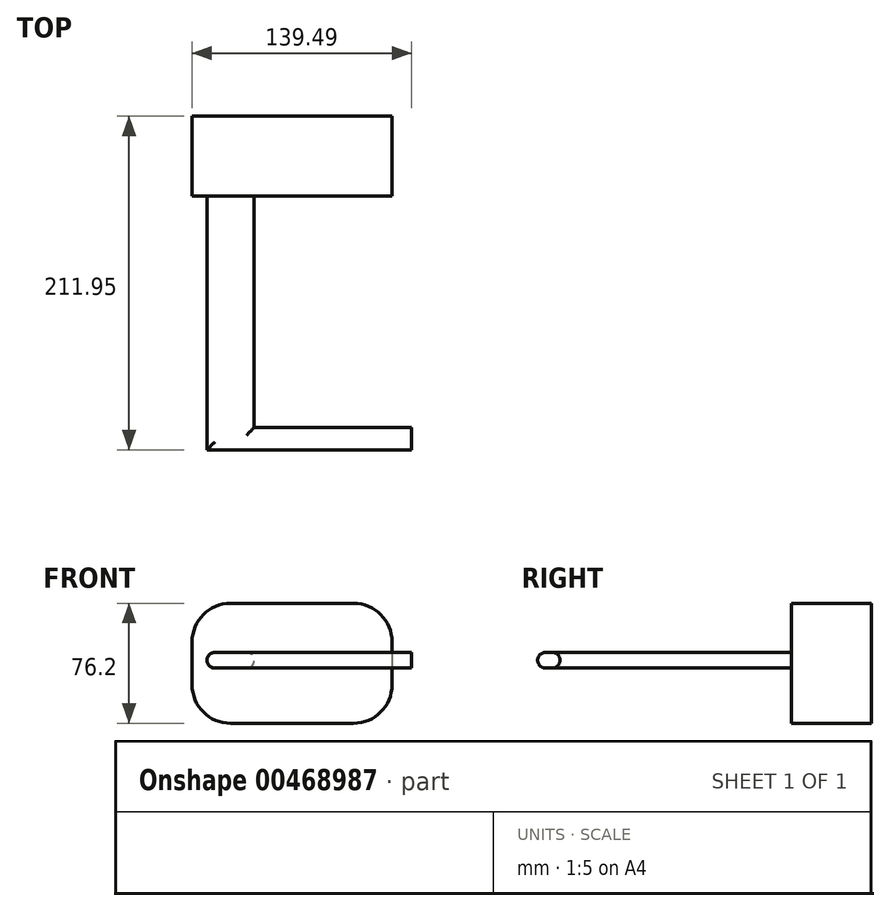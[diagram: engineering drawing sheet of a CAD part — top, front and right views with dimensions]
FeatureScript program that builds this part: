
annotation { "Feature Type Name" : "Feature", "Feature Type Description" : "" }
export const myFeature = defineFeature(function(context is Context, id is Id, definition is map)
    precondition{}
    {
        {
            var Q0;
            Q0=qCreatedBy(makeId("Front.planeOp"),FACE);
            var sketch = newSketch(context, id + "F0", { "sketchPlane" : qUnion([Q0])});
            skLineSegment(sketch, "E0.bottom", {"start": v(-41.85, 70.88) * mm, "end": v(85.15, 70.88) * mm});
            skLineSegment(sketch, "E0.top", {"start": v(-41.85, -5.32) * mm, "end": v(85.15, -5.32) * mm});
            skLineSegment(sketch, "E0.left", {"start": v(-41.85, 70.88) * mm, "end": v(-41.85, -5.32) * mm});
            skLineSegment(sketch, "E0.right", {"start": v(85.15, 70.88) * mm, "end": v(85.15, -5.32) * mm});
            skPoint(sketch, "E0.middle", {"position": v(21.65, 32.78) * mm});
            skSolve(sketch);
        }
        {
            var Q0;
            Q0=makeQuery(id+"F0.imprint","IMPRINT",FACE,{"disambiguationData":[TD([[makeQuery(id+"F0.imprint","IMPRINT",EDGE,{"derivedFrom":sQuery(id+"F0.wireOp",EDGE,"E0.bottom")}),-1.0]])]});
            extrude(context, id + "F1", {"entities" : qUnion([Q0]), "depth" : 50.8 * mm});
        }
        {
            var Q0;
            Q0=makeQuery(id+"F1.opExtrude","SWEPT_EDGE",EDGE,{"disambiguationData":[OSD([sQuery(id+"F0.wireOp",EDGE,"E0.bottom"),sQuery(id+"F0.wireOp",EDGE,"E0.left")])]});
            var Q1;
            Q1=makeQuery(id+"F1.opExtrude","SWEPT_EDGE",EDGE,{"disambiguationData":[OSD([sQuery(id+"F0.wireOp",EDGE,"E0.top"),sQuery(id+"F0.wireOp",EDGE,"E0.left")])]});
            var Q2;
            Q2=makeQuery(id+"F1.opExtrude","SWEPT_EDGE",EDGE,{"disambiguationData":[OSD([sQuery(id+"F0.wireOp",EDGE,"E0.top"),sQuery(id+"F0.wireOp",EDGE,"E0.right")])]});
            var Q3;
            Q3=makeQuery(id+"F1.opExtrude","SWEPT_EDGE",EDGE,{"disambiguationData":[OSD([sQuery(id+"F0.wireOp",EDGE,"E0.bottom"),sQuery(id+"F0.wireOp",EDGE,"E0.right")])]});
            fillet(context, id + "F2", {"entities" : qUnion([Q0, Q1, Q2, Q3]), "radius" : 24.44 * mm, "tangentPropagation" : true, "allowEdgeOverflow" : false});
        }
        {
            var Q0;
            Q0=makeQuery(id+"F1.opExtrude","CAP_FACE",FACE,{"disambiguationData":[OSD([sQuery(id+"F0.wireOp",EDGE,"E0.bottom"),sQuery(id+"F0.wireOp",EDGE,"E0.top"),sQuery(id+"F0.wireOp",EDGE,"E0.left"),sQuery(id+"F0.wireOp",EDGE,"E0.right")])],"isStart":true});
            var sketch = newSketch(context, id + "F3", { "sketchPlane" : qUnion([Q0])});
            skCircle(sketch, "E1", {"center": v(-21.77, 13.37) * mm, "radius": 18.7 * mm});
            skSolve(sketch);
        }
        {
            var Q0;
            {var subQ6=sQuery(id+"F3.wireOp",EDGE,"E1");Q0=makeQuery(id+"F3.imprint","IMPRINT",FACE,{"disambiguationData":[TD([[makeQuery(id+"F3.imprint","IMPRINT",EDGE,{"derivedFrom":subQ6}),-1.0]])]});}
            var sketch = newSketch(context, id + "F4", { "sketchPlane" : qUnion([Q0])});
            skLineSegment(sketch, "E2.bottom", {"start": v(2.36, 39.76) * mm, "end": v(32.36, 39.76) * mm});
            skLineSegment(sketch, "E2.top", {"start": v(2.36, 29.76) * mm, "end": v(32.36, 29.76) * mm});
            skLineSegment(sketch, "E2.left", {"start": v(2.36, 39.76) * mm, "end": v(2.36, 29.76) * mm});
            skLineSegment(sketch, "E2.right", {"start": v(32.36, 39.76) * mm, "end": v(32.36, 29.76) * mm});
            skSolve(sketch);
        }
        {
            var Q0;
            Q0 = qSketchRegion(id + "F4", true);
            var Q1;
            Q1=makeQuery(id+"F4.imprint","IMPRINT",FACE,{"disambiguationData":[TD([[makeQuery(id+"F4.imprint","IMPRINT",EDGE,{"derivedFrom":sQuery(id+"F4.wireOp",EDGE,"E2.bottom")}),-1.0]])]});
            extrude(context, id + "F5", {"entities" : qUnion([Q0, Q1]), "operationType" : NewBodyOperationType.ADD, "oppositeDirection" : true, "depth" : 211.95 * mm});
        }
        {
            var Q0;
            Q0=makeQuery(id+"F5.opExtrude","SWEPT_FACE",FACE,{"disambiguationData":[OSD([sQuery(id+"F4.wireOp",EDGE,"E2.left")])]});
            var sketch = newSketch(context, id + "F6", { "sketchPlane" : qUnion([Q0])});
            skLineSegment(sketch, "E3", {"start": v(-197.73, 39.76) * mm, "end": v(-197.73, 29.76) * mm});
            skSolve(sketch);
        }
        {
            var Q0;
            {var subQ0=sQuery(id+"F6.wireOp",EDGE,"E3");Q0=makeQuery(id+"F6.imprint","IMPRINT",FACE,{"disambiguationData":[TD([[makeQuery(id+"F6.imprint","IMPRINT",EDGE,{"derivedFrom":subQ0}),-1.0]])]});}
            extrude(context, id + "F7", {"entities" : qUnion([Q0]), "operationType" : NewBodyOperationType.ADD, "depth" : 100 * mm});
        }
        {
            var Q0;
            Q0=makeQuery(id+"F5.opExtrude","SWEPT_EDGE",EDGE,{"disambiguationData":[OSD([sQuery(id+"F4.wireOp",EDGE,"E2.bottom"),sQuery(id+"F4.wireOp",EDGE,"E2.right")])]});
            var Q1;
            Q1=makeQuery(id+"F5.opExtrude","SWEPT_EDGE",EDGE,{"disambiguationData":[OSD([sQuery(id+"F4.wireOp",EDGE,"E2.top"),sQuery(id+"F4.wireOp",EDGE,"E2.right")])]});
            var Q2;
            {var subQ0=sQuery(id+"F4.wireOp",EDGE,"E2.top");Q2=makeQuery(id+"F7.boolean.opBoolean","MERGE",EDGE,{"derivedFrom":[makeQuery(id+"F5.opExtrude","CAP_EDGE",EDGE,{"disambiguationData":[OSD([subQ0])],"isStart":false}),makeQuery(id+"F7.opExtrude","SWEPT_EDGE",EDGE,{"disambiguationData":[OSD([subQ0,sQuery(id+"F4.wireOp",EDGE,"E2.left")])]})]});}
            var Q3;
            Q3=makeQuery(id+"F5.opExtrude","SWEPT_EDGE",EDGE,{"disambiguationData":[OSD([sQuery(id+"F4.wireOp",EDGE,"E2.top"),sQuery(id+"F4.wireOp",EDGE,"E2.left")])]});
            var Q4;
            Q4=makeQuery(id+"F5.opExtrude","SWEPT_EDGE",EDGE,{"disambiguationData":[OSD([sQuery(id+"F4.wireOp",EDGE,"E2.bottom"),sQuery(id+"F4.wireOp",EDGE,"E2.left")])]});
            var Q5;
            Q5=makeQuery(id+"F7.opExtrude","SWEPT_EDGE",EDGE,{"disambiguationData":[OSD([sQuery(id+"F4.wireOp",EDGE,"E2.bottom"),sQuery(id+"F4.wireOp",EDGE,"E2.left"),sQuery(id+"F6.wireOp",EDGE,"E3")])]});
            var Q6;
            {var subQ0=sQuery(id+"F4.wireOp",EDGE,"E2.bottom");Q6=makeQuery(id+"F7.boolean.opBoolean","MERGE",EDGE,{"derivedFrom":[makeQuery(id+"F5.opExtrude","CAP_EDGE",EDGE,{"disambiguationData":[OSD([subQ0])],"isStart":false}),makeQuery(id+"F7.opExtrude","SWEPT_EDGE",EDGE,{"disambiguationData":[OSD([subQ0,sQuery(id+"F4.wireOp",EDGE,"E2.left")])]})]});}
            var Q7;
            Q7=makeQuery(id+"F7.opExtrude","SWEPT_EDGE",EDGE,{"disambiguationData":[OSD([sQuery(id+"F4.wireOp",EDGE,"E2.top"),sQuery(id+"F4.wireOp",EDGE,"E2.left"),sQuery(id+"F6.wireOp",EDGE,"E3")])]});
            fillet(context, id + "F8", {"entities" : qUnion([Q0, Q1, Q2, Q3, Q4, Q5, Q6, Q7]), "radius" : 5 * mm, "tangentPropagation" : true, "allowEdgeOverflow" : false});
        }
    });
